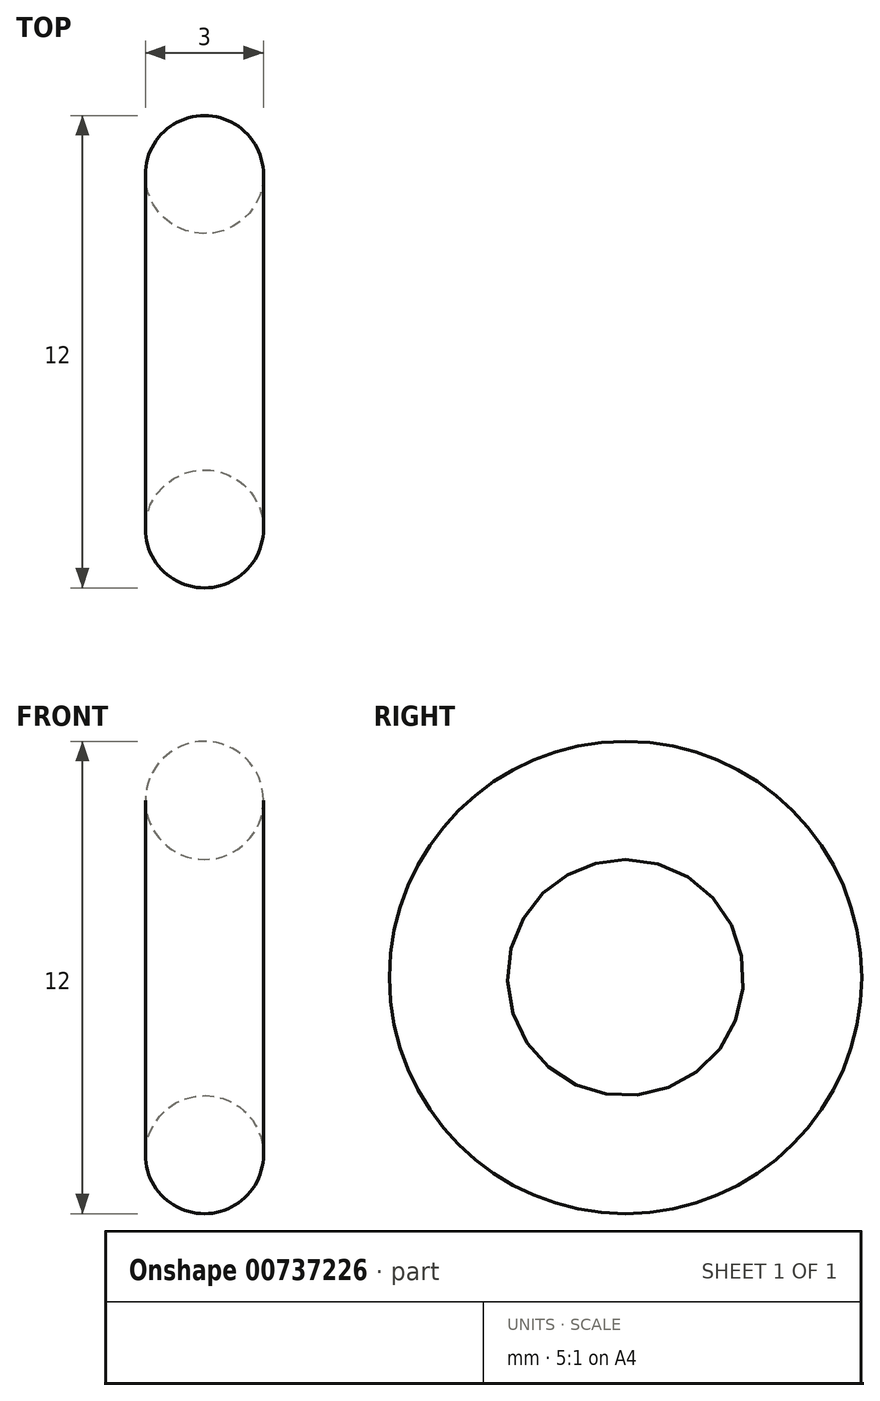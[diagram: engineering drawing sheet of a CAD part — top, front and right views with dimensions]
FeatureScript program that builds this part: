
annotation { "Feature Type Name" : "Feature", "Feature Type Description" : "" }
export const myFeature = defineFeature(function(context is Context, id is Id, definition is map)
    precondition{}
    {
        {
            var Q0;
            Q0=qCreatedBy(makeId("Front.planeOp"),FACE);
            var sketch = newSketch(context, id + "F0", { "sketchPlane" : qUnion([Q0])});
            skLineSegment(sketch, "E0", {"start": v(0, 0) * mm, "end": v(11.91, 0) * mm, "construction": true});
            skCircle(sketch, "E1", {"center": v(0, 4.5) * mm, "radius": 1.5 * mm});
            skLineSegment(sketch, "E2", {"start": v(0, 4.5) * mm, "end": v(0, 0) * mm, "construction": true});
            skPoint(sketch, "E3", {"position": v(0, 3) * mm});
            skSolve(sketch);
        }
        {
            var Q0;
            Q0=makeQuery(id+"F0.imprint","IMPRINT",FACE,{"disambiguationData":[TD([[makeQuery(id+"F0.imprint","IMPRINT",EDGE,{"derivedFrom":sQuery(id+"F0.wireOp",EDGE,"E1")}),1.0]])]});
            var Q1;
            Q1=sQuery(id+"F0.wireOp",EDGE,"E0");
            revolve(context, id + "F1", {"surfaceOperationType" : NewSurfaceOperationType.NEW, "entities" : qUnion([Q0]), "axis" : qUnion([Q1]), "revolveType" : RevolveType.FULL});
        }
    });
